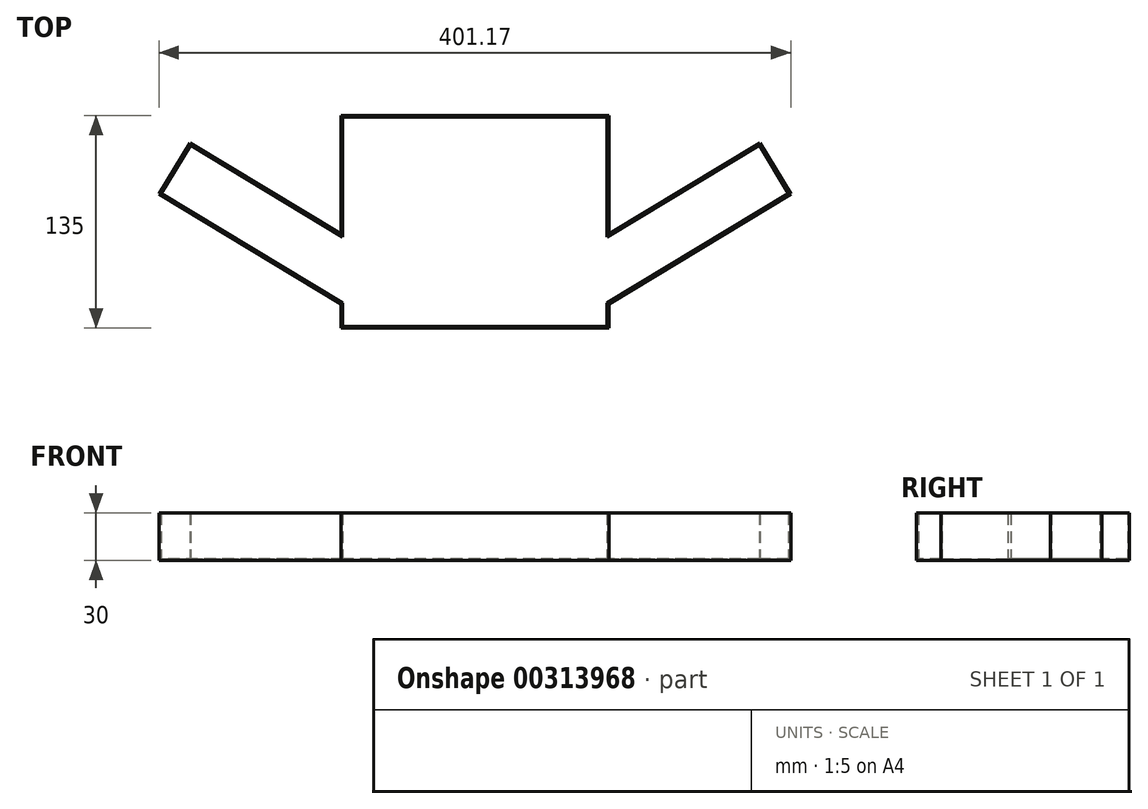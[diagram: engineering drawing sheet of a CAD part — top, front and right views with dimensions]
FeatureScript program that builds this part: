
annotation { "Feature Type Name" : "Feature", "Feature Type Description" : "" }
export const myFeature = defineFeature(function(context is Context, id is Id, definition is map)
    precondition{}
    {
        {
            var Q0;
            Q0=qCreatedBy(makeId("Top.planeOp"),FACE);
            var sketch = newSketch(context, id + "F0", { "sketchPlane" : qUnion([Q0])});
            skLineSegment(sketch, "E0.bottom", {"start": v(62.69, 66.87) * mm, "end": v(-107.31, 66.87) * mm});
            skLineSegment(sketch, "E0.top", {"start": v(62.69, -68.13) * mm, "end": v(-107.31, -68.13) * mm});
            skLineSegment(sketch, "E0.left", {"start": v(62.69, 66.87) * mm, "end": v(62.69, -68.13) * mm});
            skLineSegment(sketch, "E0.right", {"start": v(-107.31, 66.87) * mm, "end": v(-107.31, -68.13) * mm});
            skLineSegment(sketch, "E1", {"start": v(-22.31, 130.35) * mm, "end": v(-22.31, 78.75) * mm, "construction": true});
            skLineSegment(sketch, "E2", {"start": v(-105.31, 45.87) * mm, "end": v(-107.31, 45.87) * mm});
            skLineSegment(sketch, "E3", {"start": v(-108.85, 68.06) * mm, "end": v(-110.78, 68.06) * mm});
            skLineSegment(sketch, "E4", {"start": v(62.69, -52.81) * mm, "end": v(178.27, 16.94) * mm});
            skLineSegment(sketch, "E5", {"start": v(178.27, 16.94) * mm, "end": v(158.64, 49.47) * mm});
            skLineSegment(sketch, "E6", {"start": v(158.64, 49.47) * mm, "end": v(62.69, -8.43) * mm});
            skLineSegment(sketch, "E7.MirrorCS", {"start": v(-203.26, 49.47) * mm, "end": v(-107.31, -8.43) * mm});
            skLineSegment(sketch, "E8.MirrorCS", {"start": v(-107.31, -52.81) * mm, "end": v(-222.9, 16.94) * mm});
            skLineSegment(sketch, "E9.MirrorCS", {"start": v(-222.9, 16.94) * mm, "end": v(-203.26, 49.47) * mm});
            skSolve(sketch);
        }
        {
            var Q0;
            Q0 = qSketchRegion(id + "F0", true);
            extrude(context, id + "F1", {"entities" : qUnion([Q0]), "depth" : 30 * mm});
        }
        {
            var Q0;
            Q0=makeQuery(id+"F1.opExtrude","CAP_FACE",FACE,{"disambiguationData":[OSD([sQuery(id+"F0.wireOp",EDGE,"E0.bottom"),sQuery(id+"F0.wireOp",EDGE,"E0.top"),sQuery(id+"F0.wireOp",EDGE,"E0.left"),sQuery(id+"F0.wireOp",EDGE,"E0.right"),sQuery(id+"F0.wireOp",EDGE,"E4"),sQuery(id+"F0.wireOp",EDGE,"E5"),sQuery(id+"F0.wireOp",EDGE,"E6"),sQuery(id+"F0.wireOp",EDGE,"E7.MirrorCS"),sQuery(id+"F0.wireOp",EDGE,"E8.MirrorCS"),sQuery(id+"F0.wireOp",EDGE,"E9.MirrorCS")])],"isStart":false});
            shell(context, id + "F2", {"entities" : qUnion([Q0]), "thickness" : 1 * mm});
        }
    });
